# Revit family: Exhaust_Fan-Panasonic-Whisper_Green_Select-(FV-1115VK2)
name_source: partatom
category: Mechanical Equipment
revit_build: Autodesk Revit 2016 (Build: 20151007_0715(x64)
units: mm (PartAtom-declared; Revit-internal decimal feet)

## family parameters
Cut with Voids When Loaded = Yes
Host = Face
OmniClass Number = 23.75.35.17.17
OmniClass Title = Room Air Circulation Fans
Part Type = Normal
Room Calculation Point = No
Round Connector Dimension = Use Radius
Shared = Yes

## types (6) — shared parameters
Code Compliances = Can be used to comply with ASHRAE 62.2, LEED, ENERGY STAR® IAP, EarthCraft, California Title-24 and WA Ventilation Code.
Condensation Sensor = Yes
Condensation Sensor Note = Turns the fan on for 20 minutes when excess humidity is detected
Cover Finish = Plastic - Panasonic - White
Default Elevation = 4' - 0"
Description = WhisperGreen Select™ One Fan - Multiple IAQ Solutions, 50-80-110 CFM (pre-installed multi-speed)
Distributor Locator = http://www.easylocator.net
Electrical Connector = Electrical Connection
Exhaust Connector = Exhaust Connection
Exhaust Diameter = 0' - 4"
Exhaust Radius = 0' - 2"
Fan Body Finish = Metal - Panasonic - Steel
Frequency = 60 Hz
Length = 1' - 1"
Manufacturer = Panasonic
Motion Sensor = Yes
Motion Sensor Note = Turns the fan on for 20 minutes when motion is detected
Multi Speed Note = One receptacle is dedicated to Multi-Speed
Multi-Speed = Yes
Noise = 0.3
Number of Poles = 1
Phase = 1
Power Factor = 1
Product Documentation Link = ftp://ftp.panasonic.com/ventilationfan/sellsheet/whispergreen_select_sellsheet.pdf
Product Name = WhisperGreen Select™
Product Page URL = https://na.panasonic.com
URL = http://us.panasonic.com
Voltage = 120 V
Wall Thickness = 0' - 0 1/2"
Width = 1' - 1"
Wiring Manual = Fan has different wiring methods. Review wiring diagram

## per-type parameters (varying)
| type | Air Volume | Fan Wattage | Height | Speed |
| FV-1115VK2-4-50CFM-740RPM-3.5W | 50 CFM | 4 W | 0' - 8 11/16" | 740 |
| FV-1115VK2-4-80CFM-795RPM-5.5W | 80 CFM | 6 W | 0' - 8 11/16" | 795 |
| FV-1115VK2-4-110CFM-915RPM-9.5W | 110 CFM | 10 W | 0' - 7 3/8" | 915 |
| FV-1115VK2-6-50CFM-740RPM-3.5W | 50 CFM | 4 W | 0' - 8 11/16" | 740 |
| FV-1115VK2-6-80CFM-795RPM-5.5W | 80 CFM | 6 W | 0' - 8 11/16" | 795 |
| FV-1115VK2-6-110CFM-915RPM-9.5W | 110 CFM | 10 W | 0' - 8 11/16" | 915 |

note: column(s) folded — value = type name in every type: Model

## geometry (parser evidence)
native form markers: Blend x8, Sweep x3
no freeform markers — native parametric forms only
